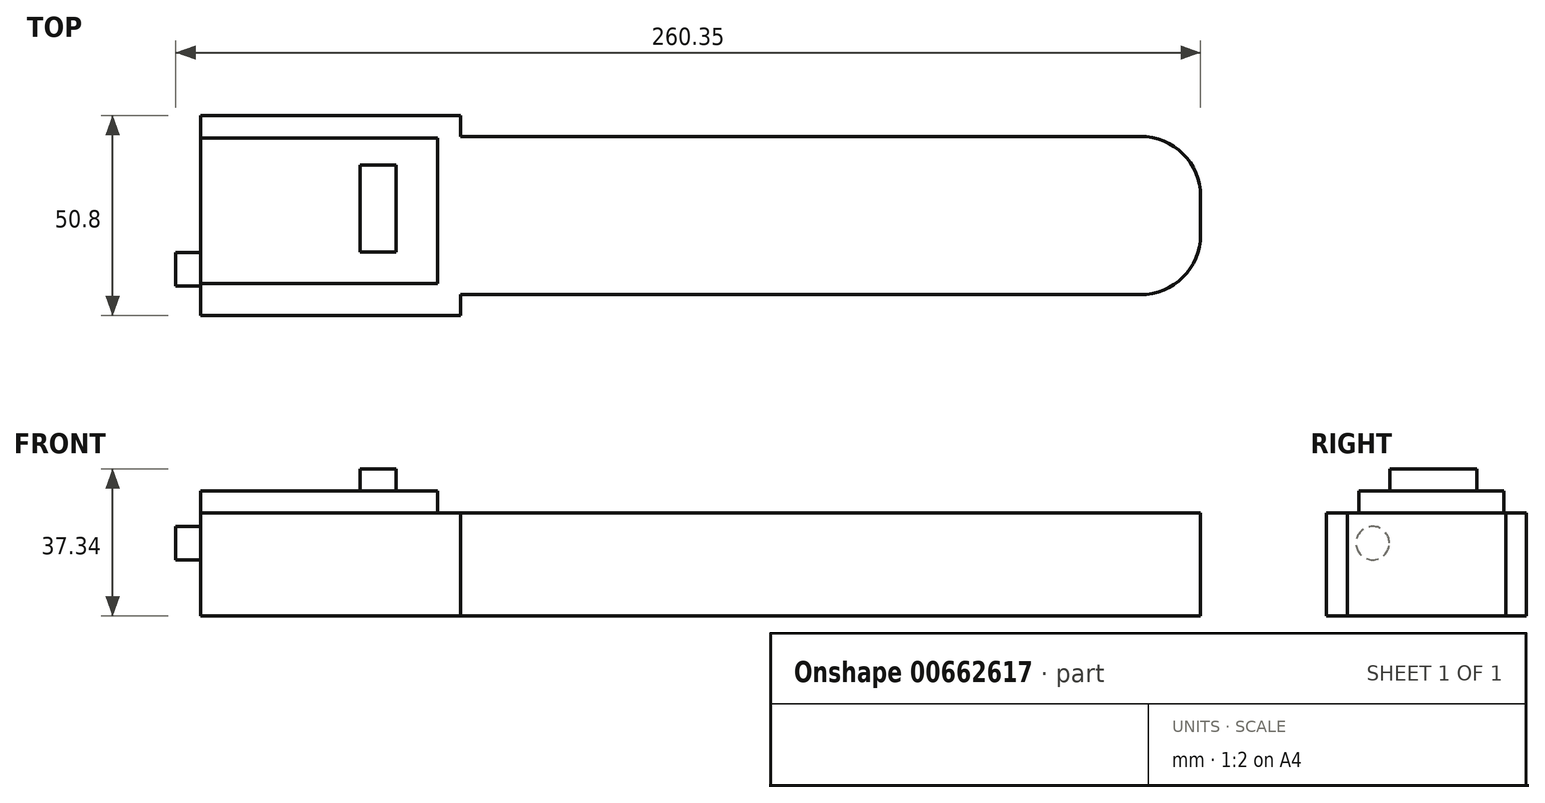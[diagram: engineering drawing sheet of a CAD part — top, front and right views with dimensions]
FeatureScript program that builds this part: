
annotation { "Feature Type Name" : "Feature", "Feature Type Description" : "" }
export const myFeature = defineFeature(function(context is Context, id is Id, definition is map)
    precondition{}
    {
        {
            var Q0;
            Q0=qCreatedBy(makeId("Top.planeOp"),FACE);
            var sketch = newSketch(context, id + "F0", { "sketchPlane" : qUnion([Q0])});
            skLineSegment(sketch, "E0.bottom", {"start": v(127, -25.4) * mm, "end": v(-127, -25.4) * mm});
            skLineSegment(sketch, "E0.top", {"start": v(127, 25.4) * mm, "end": v(-127, 25.4) * mm});
            skLineSegment(sketch, "E0.left", {"start": v(127, -25.4) * mm, "end": v(127, 25.4) * mm});
            skLineSegment(sketch, "E0.right", {"start": v(-127, -25.4) * mm, "end": v(-127, 25.4) * mm});
            skPoint(sketch, "E0.middle", {"position": v(0, 0) * mm});
            skLineSegment(sketch, "E1", {"start": v(-60.96, 25.4) * mm, "end": v(-60.96, 20.12) * mm});
            skLineSegment(sketch, "E2", {"start": v(-60.96, 20.12) * mm, "end": v(127, 20.12) * mm});
            skLineSegment(sketch, "E3", {"start": v(176.43, 0) * mm, "end": v(-172.8, 0) * mm, "construction": true});
            skLineSegment(sketch, "E4.MirrorCS", {"start": v(-60.96, -25.4) * mm, "end": v(-60.96, -20.12) * mm});
            skLineSegment(sketch, "E5.MirrorCS", {"start": v(-60.96, -20.12) * mm, "end": v(127, -20.12) * mm});
            skSolve(sketch);
        }
        {
            var Q0;
            {var subQ0=sQuery(id+"F0.wireOp",EDGE,"E0.right");Q0=makeQuery(id+"F0.imprint","IMPRINT",FACE,{"disambiguationData":[TD([[makeQuery(id+"F0.imprint","IMPRINT",EDGE,{"derivedFrom":subQ0}),-1.0]])]});}
            extrude(context, id + "F1", {"entities" : qUnion([Q0]), "depth" : 26.16 * mm, "offsetDistance" : 25.4 * mm});
        }
        {
            var Q0;
            Q0=makeQuery(id+"F1.opExtrude","SWEPT_FACE",FACE,{"disambiguationData":[OSD([sQuery(id+"F0.wireOp",EDGE,"E0.right")])]});
            var sketch = newSketch(context, id + "F2", { "sketchPlane" : qUnion([Q0])});
            skCircle(sketch, "E6", {"center": v(13.66, 18.5) * mm, "radius": 4.24 * mm});
            skSolve(sketch);
        }
        {
            var Q0;
            Q0=makeQuery(id+"F2.imprint","IMPRINT",FACE,{"disambiguationData":[TD([[makeQuery(id+"F2.imprint","IMPRINT",EDGE,{"derivedFrom":sQuery(id+"F2.wireOp",EDGE,"E6")}),1.0]])]});
            extrude(context, id + "F3", {"entities" : qUnion([Q0]), "operationType" : NewBodyOperationType.ADD, "depth" : 6.35 * mm, "offsetDistance" : 25.4 * mm});
        }
        {
            var Q0;
            Q0=makeQuery(id+"F1.opExtrude","CAP_FACE",FACE,{"disambiguationData":[OSD([sQuery(id+"F0.wireOp",EDGE,"E0.bottom"),sQuery(id+"F0.wireOp",EDGE,"E0.top"),sQuery(id+"F0.wireOp",EDGE,"E0.left"),sQuery(id+"F0.wireOp",EDGE,"E0.right"),sQuery(id+"F0.wireOp",EDGE,"E1"),sQuery(id+"F0.wireOp",EDGE,"E2"),sQuery(id+"F0.wireOp",EDGE,"E4.MirrorCS"),sQuery(id+"F0.wireOp",EDGE,"E5.MirrorCS")])],"isStart":false});
            var sketch = newSketch(context, id + "F4", { "sketchPlane" : qUnion([Q0])});
            skLineSegment(sketch, "E7.bottom", {"start": v(-127, 19.67) * mm, "end": v(-66.82, 19.67) * mm});
            skLineSegment(sketch, "E7.top", {"start": v(-127, -17.23) * mm, "end": v(-66.82, -17.23) * mm});
            skLineSegment(sketch, "E7.left", {"start": v(-127, 19.67) * mm, "end": v(-127, -17.23) * mm});
            skLineSegment(sketch, "E7.right", {"start": v(-66.82, 19.67) * mm, "end": v(-66.82, 1.22) * mm});
            skLineSegment(sketch, "E8", {"start": v(-127, 1.22) * mm, "end": v(-66.82, 1.22) * mm, "construction": true});
            skLineSegment(sketch, "E9", {"start": v(-66.82, 1.22) * mm, "end": v(-66.82, -17.23) * mm});
            skSolve(sketch);
        }
        {
            var Q0;
            Q0=makeQuery(id+"F4.imprint","IMPRINT",FACE,{"disambiguationData":[TD([[makeQuery(id+"F4.imprint","IMPRINT",EDGE,{"derivedFrom":sQuery(id+"F4.wireOp",EDGE,"E7.bottom")}),-1.0]])]});
            extrude(context, id + "F5", {"entities" : qUnion([Q0]), "operationType" : NewBodyOperationType.ADD, "depth" : 5.6 * mm, "offsetDistance" : 25.4 * mm});
        }
        {
            var Q0;
            Q0=makeQuery(id+"F5.opExtrude","CAP_FACE",FACE,{"disambiguationData":[OSD([sQuery(id+"F4.wireOp",EDGE,"E7.bottom"),sQuery(id+"F4.wireOp",EDGE,"E7.top"),sQuery(id+"F4.wireOp",EDGE,"E7.left"),sQuery(id+"F4.wireOp",EDGE,"E7.right"),sQuery(id+"F4.wireOp",EDGE,"E9")])],"isStart":false});
            var sketch = newSketch(context, id + "F6", { "sketchPlane" : qUnion([Q0])});
            skLineSegment(sketch, "E10.bottom", {"start": v(-86.53, 12.77) * mm, "end": v(-77.43, 12.77) * mm});
            skLineSegment(sketch, "E10.top", {"start": v(-86.53, -9.25) * mm, "end": v(-77.43, -9.25) * mm});
            skLineSegment(sketch, "E10.left", {"start": v(-86.53, 12.77) * mm, "end": v(-86.53, -9.25) * mm});
            skLineSegment(sketch, "E10.right", {"start": v(-77.43, 12.77) * mm, "end": v(-77.43, -9.25) * mm});
            skSolve(sketch);
        }
        {
            var Q0;
            Q0=makeQuery(id+"F6.imprint","IMPRINT",FACE,{"disambiguationData":[TD([[makeQuery(id+"F6.imprint","IMPRINT",EDGE,{"derivedFrom":sQuery(id+"F6.wireOp",EDGE,"E10.bottom")}),-1.0]])]});
            extrude(context, id + "F7", {"entities" : qUnion([Q0]), "operationType" : NewBodyOperationType.ADD, "depth" : 5.6 * mm, "offsetDistance" : 25.4 * mm});
        }
        {
            var Q0;
            Q0=makeQuery(id+"F1.opExtrude","SWEPT_EDGE",EDGE,{"disambiguationData":[OSD([sQuery(id+"F0.wireOp",EDGE,"E0.left"),sQuery(id+"F0.wireOp",EDGE,"E5.MirrorCS")])]});
            var Q1;
            Q1=makeQuery(id+"F1.opExtrude","SWEPT_EDGE",EDGE,{"disambiguationData":[OSD([sQuery(id+"F0.wireOp",EDGE,"E0.left"),sQuery(id+"F0.wireOp",EDGE,"E2")])]});
            fillet(context, id + "F8", {"entities" : qUnion([Q0, Q1]), "radius" : 15.24 * mm, "tangentPropagation" : true, "allowEdgeOverflow" : false});
        }
    });
